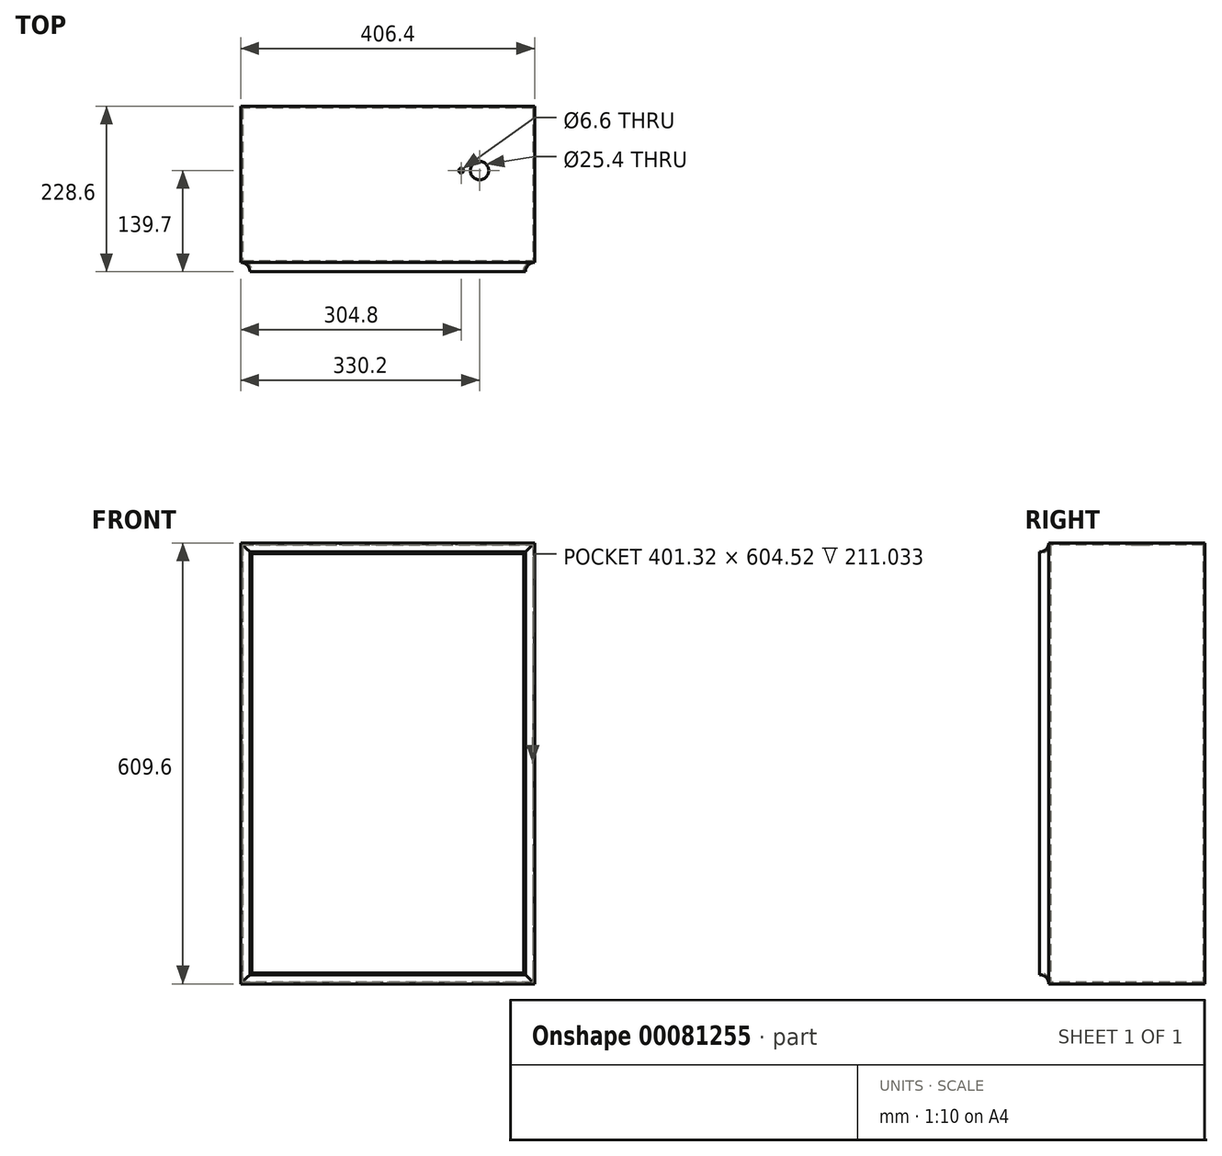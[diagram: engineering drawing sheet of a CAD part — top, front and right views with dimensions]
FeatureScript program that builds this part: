
annotation { "Feature Type Name" : "Feature", "Feature Type Description" : "" }
export const myFeature = defineFeature(function(context is Context, id is Id, definition is map)
    precondition{}
    {
        {
            var Q0;
            Q0=qCreatedBy(makeId("Top.planeOp"),FACE);
            var sketch = newSketch(context, id + "F0", { "sketchPlane" : qUnion([Q0])});
            skLineSegment(sketch, "E0.bottom", {"start": v(203.2, 114.3) * mm, "end": v(-203.2, 114.3) * mm});
            skLineSegment(sketch, "E0.top", {"start": v(190.5, -114.3) * mm, "end": v(-190.5, -114.3) * mm});
            skLineSegment(sketch, "E0.left", {"start": v(203.2, 114.3) * mm, "end": v(203.2, -101.6) * mm});
            skLineSegment(sketch, "E0.right", {"start": v(-203.2, 114.3) * mm, "end": v(-203.2, -101.6) * mm});
            skPoint(sketch, "E0.middle", {"position": v(0, 0) * mm});
            skArc(sketch, "E1", {"start": v(-190.5, -114.3) * mm, "mid": v(-194.22, -105.32) * mm, "end": v(-203.2, -101.6) * mm});
            skArc(sketch, "E2", {"start": v(203.2, -101.6) * mm, "mid": v(194.22, -105.32) * mm, "end": v(190.5, -114.3) * mm});
            skSolve(sketch);
        }
        {
            var Q0;
            Q0 = qSketchRegion(id + "F0", true);
            extrude(context, id + "F1", {"entities" : qUnion([Q0]), "depth" : 609.6 * mm});
        }
        {
            var Q0;
            Q0=makeQuery(id+"F1.opExtrude","SWEPT_FACE",FACE,{"disambiguationData":[OSD([sQuery(id+"F0.wireOp",EDGE,"E0.left")])]});
            var sketch = newSketch(context, id + "F2", { "sketchPlane" : qUnion([Q0])});
            skCircle(sketch, "E3", {"center": v(-114.3, 609.83) * mm, "radius": 12.7 * mm});
            skCircle(sketch, "E4", {"center": v(-114.3, 0) * mm, "radius": 12.7 * mm});
            skSolve(sketch);
        }
        {
            var Q0;
            Q0 = qSketchRegion(id + "F2", true);
            extrude(context, id + "F3", {"entities" : qUnion([Q0]), "operationType" : NewBodyOperationType.REMOVE, "endBound" : BoundingType.THROUGH_ALL, "oppositeDirection" : true, "depth" : 25.4 * mm});
        }
        {
            var Q0;
            Q0=makeQuery(id+"F1.opExtrude","SWEPT_FACE",FACE,{"disambiguationData":[OSD([sQuery(id+"F0.wireOp",EDGE,"E0.top")])]});
            shell(context, id + "F4", {"entities" : qUnion([Q0]), "thickness" : 2.54 * mm});
        }
        {
            var Q0;
            Q0=makeQuery(id+"F1.opExtrude","CAP_FACE",FACE,{"disambiguationData":[OSD([sQuery(id+"F0.wireOp",EDGE,"E0.bottom"),sQuery(id+"F0.wireOp",EDGE,"E0.top"),sQuery(id+"F0.wireOp",EDGE,"E0.left"),sQuery(id+"F0.wireOp",EDGE,"E0.right"),sQuery(id+"F0.wireOp",EDGE,"E1"),sQuery(id+"F0.wireOp",EDGE,"E2")])],"isStart":false});
            var sketch = newSketch(context, id + "F5", { "sketchPlane" : qUnion([Q0])});
            skCircle(sketch, "E5", {"center": v(127, 25.4) * mm, "radius": 12.7 * mm});
            skCircle(sketch, "E6", {"center": v(101.6, 25.4) * mm, "radius": 3.3 * mm});
            skSolve(sketch);
        }
        {
            var Q0;
            Q0 = qSketchRegion(id + "F5", true);
            extrude(context, id + "F6", {"entities" : qUnion([Q0]), "operationType" : NewBodyOperationType.REMOVE, "oppositeDirection" : true, "depth" : 25.4 * mm});
        }
    });
